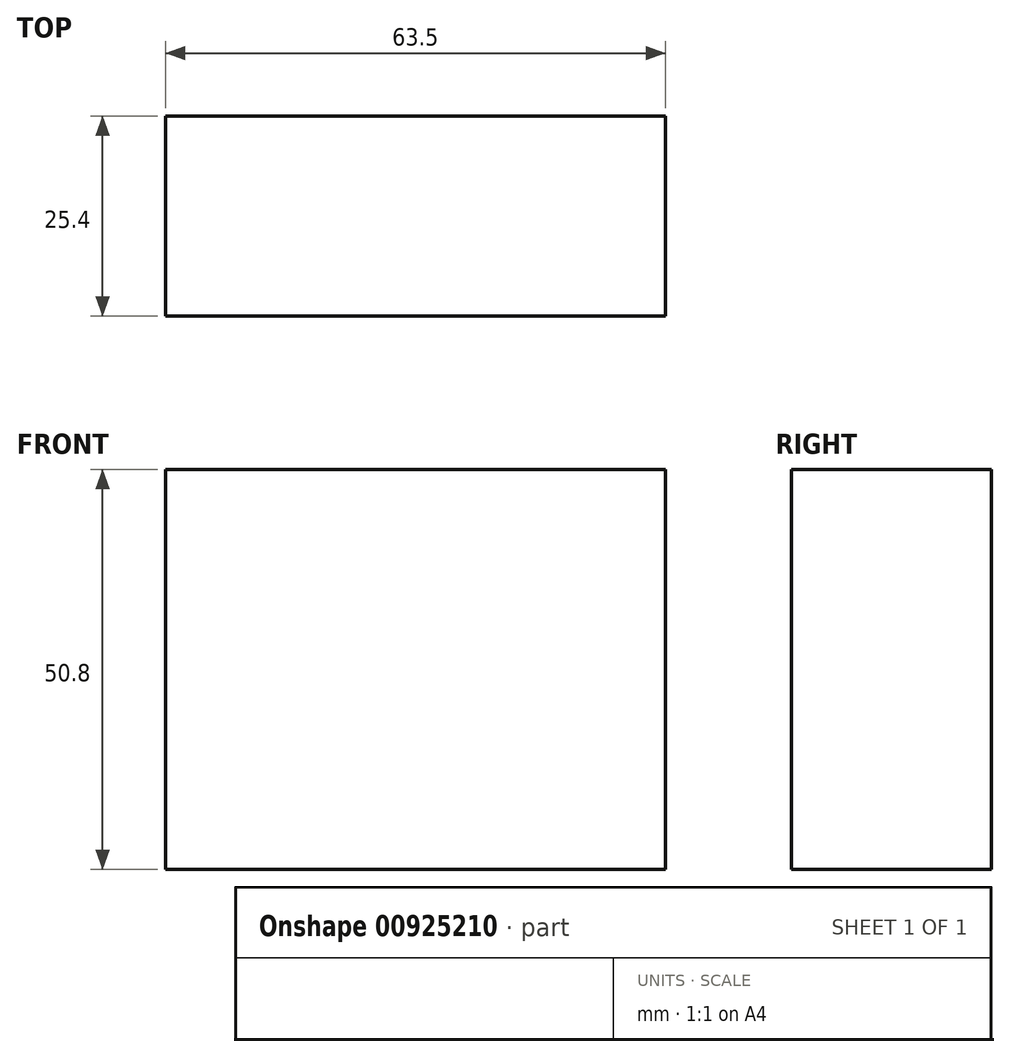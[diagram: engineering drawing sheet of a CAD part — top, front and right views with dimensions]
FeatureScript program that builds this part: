
annotation { "Feature Type Name" : "Feature", "Feature Type Description" : "" }
export const myFeature = defineFeature(function(context is Context, id is Id, definition is map)
    precondition{}
    {
        {
            var Q0;
            Q0=qCreatedBy(makeId("Top.planeOp"),FACE);
            var sketch = newSketch(context, id + "F0", { "sketchPlane" : qUnion([Q0])});
            skLineSegment(sketch, "E0.bottom", {"start": v(0, 0) * mm, "end": v(63.5, 0) * mm});
            skLineSegment(sketch, "E0.top", {"start": v(0, 25.4) * mm, "end": v(63.5, 25.4) * mm});
            skLineSegment(sketch, "E0.left", {"start": v(0, 0) * mm, "end": v(0, 25.4) * mm});
            skLineSegment(sketch, "E0.right", {"start": v(63.5, 0) * mm, "end": v(63.5, 25.4) * mm});
            skSolve(sketch);
        }
        {
            var Q0;
            Q0 = qSketchRegion(id + "F0", true);
            extrude(context, id + "F1", {"entities" : qUnion([Q0]), "depth" : 50.8 * mm, "offsetDistance" : 25.4 * mm});
        }
    });
